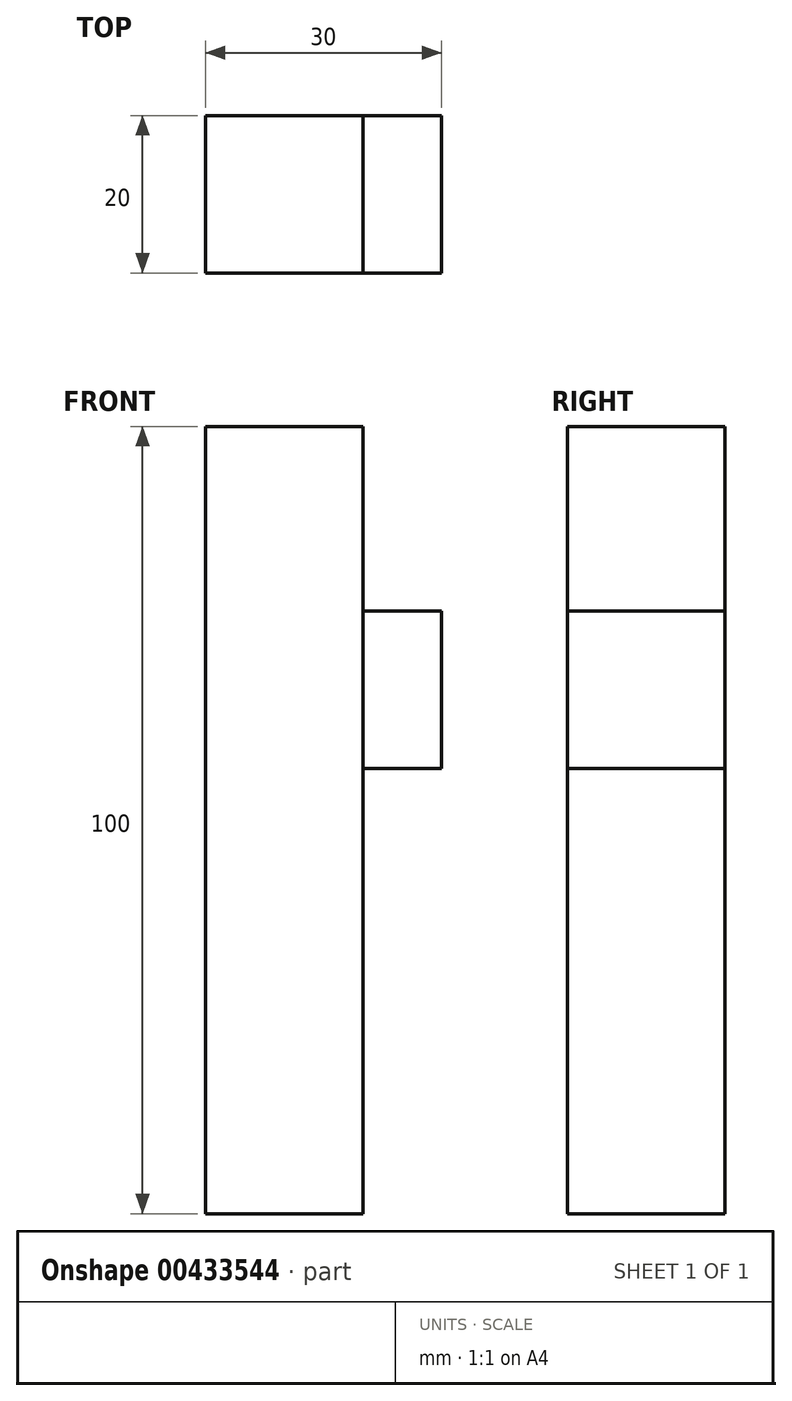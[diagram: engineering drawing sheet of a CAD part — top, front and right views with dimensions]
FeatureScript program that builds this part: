
annotation { "Feature Type Name" : "Feature", "Feature Type Description" : "" }
export const myFeature = defineFeature(function(context is Context, id is Id, definition is map)
    precondition{}
    {
        {
            var Q0;
            Q0=qCreatedBy(makeId("Top.planeOp"),FACE);
            var sketch = newSketch(context, id + "F0", { "sketchPlane" : qUnion([Q0])});
            skLineSegment(sketch, "E0.bottom", {"start": v(10, -10) * mm, "end": v(-10, -10) * mm});
            skLineSegment(sketch, "E0.top", {"start": v(10, 10) * mm, "end": v(-10, 10) * mm});
            skLineSegment(sketch, "E0.left", {"start": v(10, -10) * mm, "end": v(10, 10) * mm});
            skLineSegment(sketch, "E0.right", {"start": v(-10, -10) * mm, "end": v(-10, 10) * mm});
            skPoint(sketch, "E0.middle", {"position": v(0, 0) * mm});
            skSolve(sketch);
        }
        {
            var Q0;
            Q0=makeQuery(id+"F0.imprint","IMPRINT",FACE,{"disambiguationData":[TD([[makeQuery(id+"F0.imprint","IMPRINT",EDGE,{"derivedFrom":sQuery(id+"F0.wireOp",EDGE,"E0.bottom")}),-1.0]])]});
            extrude(context, id + "F1", {"entities" : qUnion([Q0]), "depth" : 100 * mm});
        }
        {
            var Q0;
            Q0=makeQuery(id+"F1.opExtrude","SWEPT_FACE",FACE,{"disambiguationData":[OSD([sQuery(id+"F0.wireOp",EDGE,"E0.left")])]});
            var sketch = newSketch(context, id + "F2", { "sketchPlane" : qUnion([Q0])});
            skLineSegment(sketch, "E1.bottom", {"start": v(10, 56.54) * mm, "end": v(-10, 56.54) * mm});
            skLineSegment(sketch, "E1.top", {"start": v(10, 76.54) * mm, "end": v(-10, 76.54) * mm});
            skLineSegment(sketch, "E1.left", {"start": v(10, 56.54) * mm, "end": v(10, 76.54) * mm});
            skLineSegment(sketch, "E1.right", {"start": v(-10, 56.54) * mm, "end": v(-10, 76.54) * mm});
            skPoint(sketch, "E1.middle", {"position": v(0, 66.54) * mm});
            skSolve(sketch);
        }
        {
            var Q0;
            Q0=makeQuery(id+"F2.imprint","IMPRINT",FACE,{"disambiguationData":[TD([[makeQuery(id+"F2.imprint","IMPRINT",EDGE,{"derivedFrom":sQuery(id+"F2.wireOp",EDGE,"E1.bottom")}),-1.0]])]});
            extrude(context, id + "F3", {"entities" : qUnion([Q0]), "depth" : 10 * mm});
        }
    });
